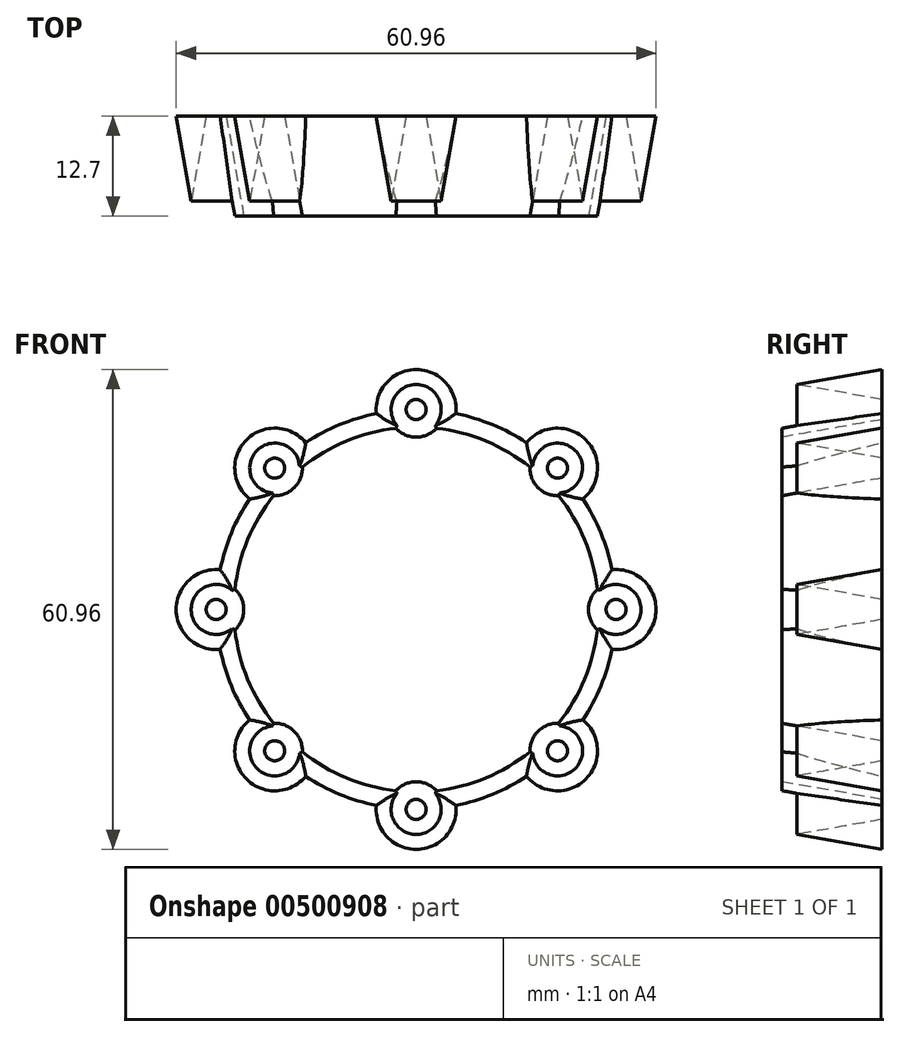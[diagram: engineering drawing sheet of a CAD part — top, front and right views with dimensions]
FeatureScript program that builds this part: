
annotation { "Feature Type Name" : "Feature", "Feature Type Description" : "" }
export const myFeature = defineFeature(function(context is Context, id is Id, definition is map)
    precondition{}
    {
        {
            var Q0;
            Q0=qCreatedBy(makeId("Front.planeOp"),FACE);
            var sketch = newSketch(context, id + "F0", { "sketchPlane" : qUnion([Q0])});
            skArc(sketch, "E0", {"start": v(-5.05, 24.9) * mm, "mid": v(-9.72, 23.47) * mm, "end": v(-14.03, 21.18) * mm});
            skLineSegment(sketch, "E1", {"start": v(0, 0) * mm, "end": v(17.96, -17.96) * mm, "construction": true});
            skLineSegment(sketch, "E2", {"start": v(0, 0) * mm, "end": v(17.96, 17.96) * mm, "construction": true});
            skArc(sketch, "E3", {"start": v(5.05, 24.9) * mm, "mid": v(0, 30.48) * mm, "end": v(-5.05, 24.9) * mm});
            skArc(sketch, "E4.1.0", {"start": v(-14.03, 21.18) * mm, "mid": v(-21.55, 21.55) * mm, "end": v(-21.18, 14.03) * mm});
            skArc(sketch, "E4.2.0", {"start": v(-24.9, 5.05) * mm, "mid": v(-30.48, 0) * mm, "end": v(-24.9, -5.05) * mm});
            skArc(sketch, "E4.3.0", {"start": v(-21.18, -14.03) * mm, "mid": v(-21.55, -21.55) * mm, "end": v(-14.03, -21.18) * mm});
            skArc(sketch, "E4.4.0", {"start": v(-5.05, -24.9) * mm, "mid": v(0, -30.48) * mm, "end": v(5.05, -24.9) * mm});
            skArc(sketch, "E4.5.0", {"start": v(14.03, -21.18) * mm, "mid": v(21.55, -21.55) * mm, "end": v(21.18, -14.03) * mm});
            skArc(sketch, "E4.6.0", {"start": v(24.9, -5.05) * mm, "mid": v(30.48, 0) * mm, "end": v(24.9, 5.05) * mm});
            skArc(sketch, "E4.7.0", {"start": v(21.18, 14.03) * mm, "mid": v(21.55, 21.55) * mm, "end": v(14.03, 21.18) * mm});
            skArc(sketch, "E5.trimOffspring", {"start": v(-21.18, 14.03) * mm, "mid": v(-23.47, 9.72) * mm, "end": v(-24.9, 5.05) * mm});
            skArc(sketch, "E6.trimOffspring", {"start": v(-24.9, -5.05) * mm, "mid": v(-23.47, -9.72) * mm, "end": v(-21.18, -14.03) * mm});
            skArc(sketch, "E7.trimOffspring", {"start": v(-14.03, -21.18) * mm, "mid": v(-9.72, -23.47) * mm, "end": v(-5.05, -24.9) * mm});
            skArc(sketch, "E8.trimOffspring", {"start": v(5.05, -24.9) * mm, "mid": v(9.72, -23.47) * mm, "end": v(14.03, -21.18) * mm});
            skArc(sketch, "E9.trimOffspring", {"start": v(21.18, -14.03) * mm, "mid": v(23.47, -9.72) * mm, "end": v(24.9, -5.05) * mm});
            skArc(sketch, "E10.trimOffspring", {"start": v(24.9, 5.05) * mm, "mid": v(23.47, 9.72) * mm, "end": v(21.18, 14.03) * mm});
            skArc(sketch, "E11.trimOffspring", {"start": v(14.03, 21.18) * mm, "mid": v(9.72, 23.47) * mm, "end": v(5.05, 24.9) * mm});
            skCircle(sketch, "E12", {"center": v(0, 25.4) * mm, "radius": 1.27 * mm});
            skCircle(sketch, "E13.1.0", {"center": v(-17.96, 17.96) * mm, "radius": 1.27 * mm});
            skCircle(sketch, "E13.2.0", {"center": v(-25.4, 0) * mm, "radius": 1.27 * mm});
            skCircle(sketch, "E13.3.0", {"center": v(-17.96, -17.96) * mm, "radius": 1.27 * mm});
            skCircle(sketch, "E13.4.0", {"center": v(0, -25.4) * mm, "radius": 1.27 * mm});
            skCircle(sketch, "E13.5.0", {"center": v(17.96, -17.96) * mm, "radius": 1.27 * mm});
            skCircle(sketch, "E13.6.0", {"center": v(25.4, 0) * mm, "radius": 1.27 * mm});
            skCircle(sketch, "E13.7.0", {"center": v(17.96, 17.96) * mm, "radius": 1.27 * mm});
            skSolve(sketch);
        }
        {
            var Q0;
            Q0=makeQuery(id+"F0.imprint","IMPRINT",FACE,{"disambiguationData":[TD([[makeQuery(id+"F0.imprint","IMPRINT",EDGE,{"derivedFrom":sQuery(id+"F0.wireOp",EDGE,"E0")}),1.0]])]});
            extrude(context, id + "F1", {"entities" : qUnion([Q0]), "flatOperationType" : FlatOperationType.REMOVE, "offsetDistance" : 25.4 * mm, "depth" : 12.7 * mm, "hasDraft" : true, "draftAngle" : 10 * degree, "draftPullDirection" : true, "domain" : OperationDomain.MODEL});
        }
    });
